# Revit family: Goalpost_PerfectGoal_Gooseneck
name_source: partatom
category: Site
units: mm (PartAtom-declared; Revit-internal decimal feet)

## family parameters
Always vertical = Yes
Cut with Voids When Loaded = No
OmniClass Number = 23.40.50.34.14
OmniClass Title = Gymnasium Equipment
Part Type = Normal
Round Connector Dimension = Use Diameter
Shared = No
Work Plane-Based = No

## types (6) — shared parameters
Building Codes = https://www.brpbybison.com
Construction Details = https://www.arcat.com
Description = IPI by Bison Gymnasium Equipment
Embedding Depth = 4' - 0"
Goal Post Finish = Powder Coat - Specify Color
Green Building-LEED = https://www.arcat.com
Installation-Fabrication = http://www.ipibybison.com
Keynote = 11 66 00
Manufacturer = BRP by bison
Manufacturer Fax = 888-438-5312
Manufacturer Website = http://www.ipibybison.com
Model = As Specified
Post Height = 20' - 0"
Product Data = http://www.arcat.com
Rail Elevation = 10' - 0"
Revision = R1_2018-09
Sales Information = http://www.ipibybison.com
Specification = https://www.arcat.com
Test Data = http://www.ipibybison.com
Total Height = 29' - 7 1/2"
URL = https://ipibybison.com

## per-type parameters (varying)
| type | Goal Clearance | Gooseneck Diameter | Setback | Total Width |
| FB45HS | 23' - 4" | 0' - 4 1/2" | 5' - 0" | 23' - 8 3/4" |
| FB45CG | 18' - 6" | 0' - 4 1/2" | 5' - 0" | 18' - 10 3/4" |
| FB55CG | 18' - 6" | 0' - 5 9/16" | 6' - 0" | 18' - 10 3/4" |
| FB55HS | 23' - 4" | 0' - 5 9/16" | 6' - 0" | 23' - 8 3/4" |
| FB58CG | 18' - 6" | 0' - 5 9/16" | 8' - 0" | 18' - 10 3/4" |
| FB58HS | 23' - 4" | 0' - 5 9/16" | 8' - 0" | 23' - 8 3/4" |
